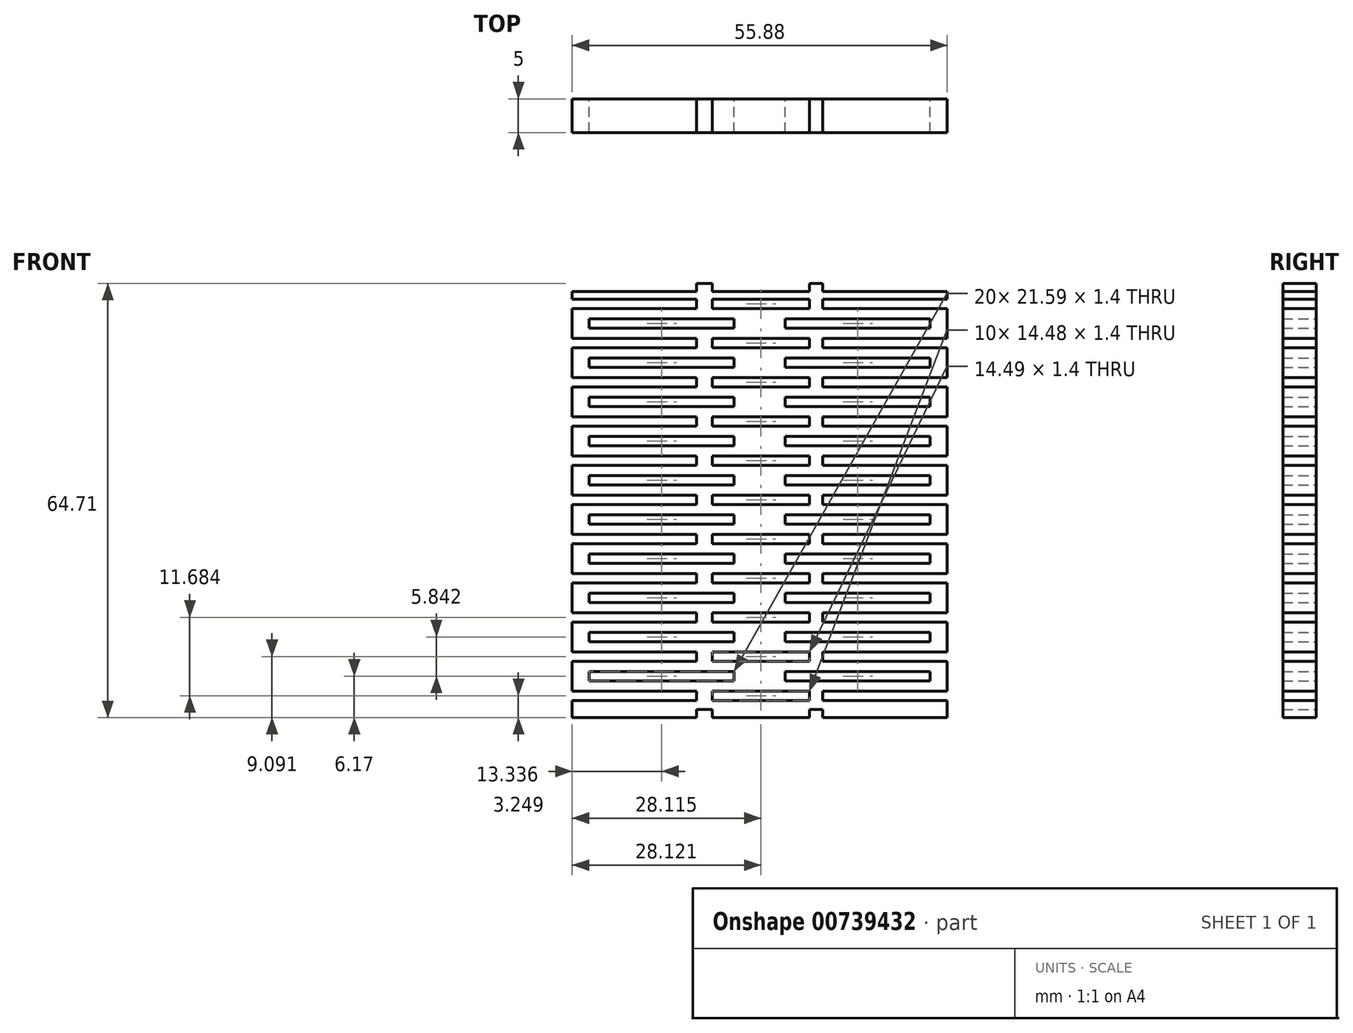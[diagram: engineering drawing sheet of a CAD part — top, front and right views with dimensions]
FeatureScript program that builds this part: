
annotation { "Feature Type Name" : "Feature", "Feature Type Description" : "" }
export const myFeature = defineFeature(function(context is Context, id is Id, definition is map)
    precondition{}
    {
        {
            var Q0;
            Q0=qCreatedBy(makeId("Front.planeOp"),FACE);
            var sketch = newSketch(context, id + "F0", { "sketchPlane" : qUnion([Q0])});
            skLineSegment(sketch, "E0", {"start": v(-42.6, 50.79) * mm, "end": v(-24.06, 50.79) * mm});
            skLineSegment(sketch, "E1", {"start": v(13.28, 50.79) * mm, "end": v(13.28, 49.63) * mm});
            skLineSegment(sketch, "E2", {"start": v(13.28, -12.71) * mm, "end": v(-5.26, -12.71) * mm});
            skLineSegment(sketch, "E3", {"start": v(-42.6, -12.71) * mm, "end": v(-42.6, -10.16) * mm});
            skPoint(sketch, "E4.start.orphan", {"position": v(-42.6, 19.04) * mm});
            skPoint(sketch, "E5.start.orphan", {"position": v(13.28, 19.04) * mm});
            skLineSegment(sketch, "E6", {"start": v(-42.6, 19.04) * mm, "end": v(-24.06, 19.04) * mm});
            skLineSegment(sketch, "E7", {"start": v(13.28, 19.04) * mm, "end": v(-5.26, 19.04) * mm});
            skLineSegment(sketch, "E8", {"start": v(-21.72, 19.04) * mm, "end": v(-7.24, 19.04) * mm});
            skLineSegment(sketch, "E9", {"start": v(-40.06, 16.13) * mm, "end": v(-18.47, 16.13) * mm});
            skLineSegment(sketch, "E10", {"start": v(10.74, 16.13) * mm, "end": v(-10.85, 16.13) * mm});
            skLineSegment(sketch, "E11", {"start": v(-24.06, 13.2) * mm, "end": v(-42.6, 13.2) * mm});
            skLineSegment(sketch, "E12", {"start": v(-21.72, 13.2) * mm, "end": v(-7.24, 13.2) * mm});
            skLineSegment(sketch, "E13", {"start": v(-5.26, 13.2) * mm, "end": v(13.28, 13.2) * mm});
            skLineSegment(sketch, "E14", {"start": v(-40.06, 10.29) * mm, "end": v(-18.47, 10.29) * mm});
            skLineSegment(sketch, "E15", {"start": v(-10.85, 10.29) * mm, "end": v(10.74, 10.29) * mm});
            skLineSegment(sketch, "E16", {"start": v(-24.06, 7.37) * mm, "end": v(-42.6, 7.37) * mm});
            skLineSegment(sketch, "E17", {"start": v(-21.72, 7.37) * mm, "end": v(-7.24, 7.37) * mm});
            skLineSegment(sketch, "E18", {"start": v(-5.26, 7.37) * mm, "end": v(13.28, 7.37) * mm});
            skLineSegment(sketch, "E19", {"start": v(-40.06, 4.45) * mm, "end": v(-18.47, 4.45) * mm});
            skLineSegment(sketch, "E20", {"start": v(-10.85, 4.45) * mm, "end": v(10.74, 4.45) * mm});
            skLineSegment(sketch, "E21", {"start": v(-24.06, 1.52) * mm, "end": v(-42.6, 1.52) * mm});
            skLineSegment(sketch, "E22", {"start": v(-21.72, 1.52) * mm, "end": v(-7.24, 1.52) * mm});
            skLineSegment(sketch, "E23", {"start": v(-5.26, 1.52) * mm, "end": v(13.28, 1.52) * mm});
            skLineSegment(sketch, "E24", {"start": v(-40.06, -1.4) * mm, "end": v(-18.47, -1.4) * mm});
            skLineSegment(sketch, "E25", {"start": v(-10.85, -1.4) * mm, "end": v(10.74, -1.4) * mm});
            skLineSegment(sketch, "E26", {"start": v(-24.06, -4.32) * mm, "end": v(-42.6, -4.32) * mm});
            skLineSegment(sketch, "E27", {"start": v(-21.72, -4.32) * mm, "end": v(-7.24, -4.32) * mm});
            skLineSegment(sketch, "E28", {"start": v(-5.26, -4.32) * mm, "end": v(13.28, -4.32) * mm});
            skLineSegment(sketch, "E29", {"start": v(-40.06, -7.24) * mm, "end": v(-18.47, -7.24) * mm});
            skLineSegment(sketch, "E30", {"start": v(-10.85, -7.24) * mm, "end": v(10.74, -7.24) * mm});
            skLineSegment(sketch, "E31", {"start": v(-24.06, -10.16) * mm, "end": v(-42.6, -10.16) * mm});
            skLineSegment(sketch, "E32", {"start": v(-21.72, -10.16) * mm, "end": v(-7.24, -10.16) * mm});
            skLineSegment(sketch, "E33", {"start": v(-5.26, -10.16) * mm, "end": v(13.28, -10.16) * mm});
            skLineSegment(sketch, "E34.MirrorCS", {"start": v(-24.06, 48.23) * mm, "end": v(-42.6, 48.23) * mm});
            skLineSegment(sketch, "E35.MirrorCS", {"start": v(-40.06, 45.31) * mm, "end": v(-18.47, 45.31) * mm});
            skLineSegment(sketch, "E36.MirrorCS", {"start": v(-24.06, 42.4) * mm, "end": v(-42.6, 42.4) * mm});
            skLineSegment(sketch, "E37.MirrorCS", {"start": v(-40.06, 39.47) * mm, "end": v(-18.47, 39.47) * mm});
            skLineSegment(sketch, "E38.MirrorCS", {"start": v(-24.06, 36.55) * mm, "end": v(-42.6, 36.55) * mm});
            skLineSegment(sketch, "E39.MirrorCS", {"start": v(-40.06, 33.63) * mm, "end": v(-18.47, 33.63) * mm});
            skLineSegment(sketch, "E40.MirrorCS", {"start": v(-24.06, 30.7) * mm, "end": v(-42.6, 30.7) * mm});
            skLineSegment(sketch, "E41.MirrorCS", {"start": v(-40.06, 27.79) * mm, "end": v(-18.47, 27.79) * mm});
            skLineSegment(sketch, "E42.MirrorCS", {"start": v(-24.06, 24.87) * mm, "end": v(-42.6, 24.87) * mm});
            skLineSegment(sketch, "E43.MirrorCS", {"start": v(-40.06, 21.95) * mm, "end": v(-18.47, 21.95) * mm});
            skLineSegment(sketch, "E44.MirrorCS", {"start": v(-21.72, 48.23) * mm, "end": v(-7.24, 48.23) * mm});
            skLineSegment(sketch, "E45.MirrorCS", {"start": v(-21.72, 42.4) * mm, "end": v(-7.24, 42.4) * mm});
            skLineSegment(sketch, "E46.MirrorCS", {"start": v(-21.72, 36.55) * mm, "end": v(-7.24, 36.55) * mm});
            skLineSegment(sketch, "E47.MirrorCS", {"start": v(-21.72, 30.7) * mm, "end": v(-7.24, 30.7) * mm});
            skLineSegment(sketch, "E48.MirrorCS", {"start": v(-21.72, 24.87) * mm, "end": v(-7.24, 24.87) * mm});
            skLineSegment(sketch, "E49.MirrorCS", {"start": v(-5.26, 48.23) * mm, "end": v(13.28, 48.23) * mm});
            skLineSegment(sketch, "E50.MirrorCS", {"start": v(-10.85, 45.31) * mm, "end": v(10.74, 45.31) * mm});
            skLineSegment(sketch, "E51.MirrorCS", {"start": v(-5.26, 42.4) * mm, "end": v(13.28, 42.4) * mm});
            skLineSegment(sketch, "E52.MirrorCS", {"start": v(-10.85, 39.47) * mm, "end": v(10.74, 39.47) * mm});
            skLineSegment(sketch, "E53.MirrorCS", {"start": v(-5.26, 36.55) * mm, "end": v(13.28, 36.55) * mm});
            skLineSegment(sketch, "E54.MirrorCS", {"start": v(-10.85, 33.63) * mm, "end": v(10.74, 33.63) * mm});
            skLineSegment(sketch, "E55.MirrorCS", {"start": v(-5.26, 30.7) * mm, "end": v(13.28, 30.7) * mm});
            skLineSegment(sketch, "E56.MirrorCS", {"start": v(-10.85, 27.79) * mm, "end": v(10.74, 27.79) * mm});
            skLineSegment(sketch, "E57.MirrorCS", {"start": v(-5.26, 24.87) * mm, "end": v(13.28, 24.87) * mm});
            skLineSegment(sketch, "E58.MirrorCS", {"start": v(10.74, 21.95) * mm, "end": v(-10.85, 21.95) * mm});
            skLineSegment(sketch, "E59", {"start": v(-24.06, 49.63) * mm, "end": v(-24.06, 48.23) * mm});
            skLineSegment(sketch, "E60", {"start": v(-24.06, 49.63) * mm, "end": v(-42.6, 49.63) * mm});
            skLineSegment(sketch, "E61", {"start": v(-18.47, 45.31) * mm, "end": v(-18.47, 46.71) * mm});
            skLineSegment(sketch, "E62", {"start": v(-18.47, 46.71) * mm, "end": v(-40.06, 46.71) * mm});
            skLineSegment(sketch, "E63", {"start": v(-40.06, 46.71) * mm, "end": v(-40.06, 45.31) * mm});
            skLineSegment(sketch, "E64", {"start": v(-24.06, 42.4) * mm, "end": v(-24.06, 43.79) * mm});
            skLineSegment(sketch, "E65", {"start": v(-24.06, 43.79) * mm, "end": v(-42.6, 43.79) * mm});
            skLineSegment(sketch, "E66", {"start": v(-18.47, 39.47) * mm, "end": v(-18.47, 40.87) * mm});
            skLineSegment(sketch, "E67", {"start": v(-18.47, 40.87) * mm, "end": v(-40.06, 40.87) * mm});
            skLineSegment(sketch, "E68", {"start": v(-40.06, 40.87) * mm, "end": v(-40.06, 39.47) * mm});
            skLineSegment(sketch, "E69", {"start": v(-24.06, 36.55) * mm, "end": v(-24.06, 37.95) * mm});
            skLineSegment(sketch, "E70", {"start": v(-24.06, 37.95) * mm, "end": v(-42.6, 37.95) * mm});
            skLineSegment(sketch, "E71", {"start": v(-18.47, 33.63) * mm, "end": v(-18.47, 35.03) * mm});
            skLineSegment(sketch, "E72", {"start": v(-18.47, 35.03) * mm, "end": v(-40.06, 35.03) * mm});
            skLineSegment(sketch, "E73", {"start": v(-40.06, 35.03) * mm, "end": v(-40.06, 33.63) * mm});
            skLineSegment(sketch, "E74", {"start": v(-24.06, 30.7) * mm, "end": v(-24.06, 32.12) * mm});
            skLineSegment(sketch, "E75", {"start": v(-24.06, 32.12) * mm, "end": v(-42.6, 32.12) * mm});
            skLineSegment(sketch, "E76", {"start": v(-18.47, 27.79) * mm, "end": v(-18.47, 29.18) * mm});
            skLineSegment(sketch, "E77", {"start": v(-18.47, 29.18) * mm, "end": v(-40.06, 29.18) * mm});
            skLineSegment(sketch, "E78", {"start": v(-40.06, 29.18) * mm, "end": v(-40.06, 27.79) * mm});
            skLineSegment(sketch, "E79", {"start": v(-24.06, 24.87) * mm, "end": v(-24.06, 26.26) * mm});
            skLineSegment(sketch, "E80", {"start": v(-24.06, 26.26) * mm, "end": v(-42.6, 26.26) * mm});
            skLineSegment(sketch, "E81", {"start": v(-18.47, 21.95) * mm, "end": v(-18.47, 23.34) * mm});
            skLineSegment(sketch, "E82", {"start": v(-18.47, 23.34) * mm, "end": v(-40.06, 23.34) * mm});
            skLineSegment(sketch, "E83", {"start": v(-40.06, 23.34) * mm, "end": v(-40.06, 21.95) * mm});
            skLineSegment(sketch, "E84", {"start": v(-24.06, 19.04) * mm, "end": v(-24.06, 20.43) * mm});
            skLineSegment(sketch, "E85", {"start": v(-24.06, 20.43) * mm, "end": v(-42.6, 20.43) * mm});
            skLineSegment(sketch, "E86", {"start": v(-18.47, 16.13) * mm, "end": v(-18.47, 17.53) * mm});
            skLineSegment(sketch, "E87", {"start": v(-18.47, 17.53) * mm, "end": v(-40.06, 17.53) * mm});
            skLineSegment(sketch, "E88", {"start": v(-40.06, 17.53) * mm, "end": v(-40.06, 16.13) * mm});
            skLineSegment(sketch, "E89", {"start": v(-24.06, 13.2) * mm, "end": v(-24.06, 14.6) * mm});
            skLineSegment(sketch, "E90", {"start": v(-24.06, 14.6) * mm, "end": v(-42.6, 14.6) * mm});
            skLineSegment(sketch, "E91", {"start": v(-18.47, 10.29) * mm, "end": v(-18.47, 11.68) * mm});
            skLineSegment(sketch, "E92", {"start": v(-18.47, 11.68) * mm, "end": v(-40.06, 11.68) * mm});
            skLineSegment(sketch, "E93", {"start": v(-40.06, 11.68) * mm, "end": v(-40.06, 10.29) * mm});
            skLineSegment(sketch, "E94", {"start": v(-24.06, 7.37) * mm, "end": v(-24.06, 8.76) * mm});
            skLineSegment(sketch, "E95", {"start": v(-24.06, 8.76) * mm, "end": v(-42.6, 8.76) * mm});
            skLineSegment(sketch, "E96", {"start": v(-18.47, 4.45) * mm, "end": v(-18.47, 5.84) * mm});
            skLineSegment(sketch, "E97", {"start": v(-18.47, 5.84) * mm, "end": v(-40.06, 5.84) * mm});
            skLineSegment(sketch, "E98", {"start": v(-40.06, 5.84) * mm, "end": v(-40.06, 4.45) * mm});
            skLineSegment(sketch, "E99", {"start": v(-24.06, 1.52) * mm, "end": v(-24.06, 2.92) * mm});
            skLineSegment(sketch, "E100", {"start": v(-24.06, 2.92) * mm, "end": v(-42.6, 2.92) * mm});
            skLineSegment(sketch, "E101", {"start": v(-18.47, -1.4) * mm, "end": v(-18.47, 0) * mm});
            skLineSegment(sketch, "E102", {"start": v(-18.47, 0) * mm, "end": v(-40.06, 0) * mm});
            skLineSegment(sketch, "E103", {"start": v(-40.06, 0) * mm, "end": v(-40.06, -1.4) * mm});
            skLineSegment(sketch, "E104", {"start": v(-24.06, -4.32) * mm, "end": v(-24.06, -2.92) * mm});
            skLineSegment(sketch, "E105", {"start": v(-24.06, -2.92) * mm, "end": v(-42.6, -2.92) * mm});
            skLineSegment(sketch, "E106", {"start": v(-18.47, -7.24) * mm, "end": v(-18.47, -5.84) * mm});
            skLineSegment(sketch, "E107", {"start": v(-18.47, -5.84) * mm, "end": v(-40.06, -5.84) * mm});
            skLineSegment(sketch, "E108", {"start": v(-40.06, -5.84) * mm, "end": v(-40.06, -7.24) * mm});
            skLineSegment(sketch, "E109", {"start": v(-24.06, -10.16) * mm, "end": v(-24.06, -8.76) * mm});
            skLineSegment(sketch, "E110", {"start": v(-24.06, -8.76) * mm, "end": v(-42.6, -8.76) * mm});
            skLineSegment(sketch, "E111", {"start": v(-7.24, 48.23) * mm, "end": v(-7.24, 49.63) * mm});
            skLineSegment(sketch, "E112", {"start": v(-7.24, 49.63) * mm, "end": v(-21.72, 49.63) * mm});
            skLineSegment(sketch, "E113", {"start": v(-21.72, 49.63) * mm, "end": v(-21.72, 48.23) * mm});
            skLineSegment(sketch, "E114", {"start": v(-7.24, 42.4) * mm, "end": v(-7.24, 43.79) * mm});
            skLineSegment(sketch, "E115", {"start": v(-7.24, 43.79) * mm, "end": v(-21.72, 43.79) * mm});
            skLineSegment(sketch, "E116", {"start": v(-21.72, 43.79) * mm, "end": v(-21.72, 42.4) * mm});
            skLineSegment(sketch, "E117", {"start": v(-7.24, 36.55) * mm, "end": v(-7.24, 37.95) * mm});
            skLineSegment(sketch, "E118", {"start": v(-7.24, 37.95) * mm, "end": v(-21.72, 37.95) * mm});
            skLineSegment(sketch, "E119", {"start": v(-21.72, 37.95) * mm, "end": v(-21.72, 36.55) * mm});
            skLineSegment(sketch, "E120", {"start": v(-7.24, 30.7) * mm, "end": v(-7.24, 32.1) * mm});
            skLineSegment(sketch, "E121", {"start": v(-7.24, 32.1) * mm, "end": v(-21.72, 32.1) * mm});
            skLineSegment(sketch, "E122", {"start": v(-21.72, 32.1) * mm, "end": v(-21.72, 30.7) * mm});
            skLineSegment(sketch, "E123", {"start": v(-7.24, 24.87) * mm, "end": v(-7.24, 26.26) * mm});
            skLineSegment(sketch, "E124", {"start": v(-7.24, 26.26) * mm, "end": v(-21.72, 26.26) * mm});
            skLineSegment(sketch, "E125", {"start": v(-21.72, 26.26) * mm, "end": v(-21.72, 24.87) * mm});
            skLineSegment(sketch, "E126", {"start": v(-7.24, 19.04) * mm, "end": v(-7.24, 20.43) * mm});
            skLineSegment(sketch, "E127", {"start": v(-7.24, 20.43) * mm, "end": v(-21.72, 20.43) * mm});
            skLineSegment(sketch, "E128", {"start": v(-21.72, 20.43) * mm, "end": v(-21.72, 19.04) * mm});
            skLineSegment(sketch, "E129", {"start": v(-7.24, 13.2) * mm, "end": v(-7.24, 14.6) * mm});
            skLineSegment(sketch, "E130", {"start": v(-7.24, 14.6) * mm, "end": v(-21.7, 14.6) * mm});
            skLineSegment(sketch, "E131", {"start": v(-21.7, 14.6) * mm, "end": v(-21.72, 13.2) * mm});
            skLineSegment(sketch, "E132", {"start": v(-7.24, 7.37) * mm, "end": v(-7.24, 8.76) * mm});
            skLineSegment(sketch, "E133", {"start": v(-7.24, 8.76) * mm, "end": v(-21.7, 8.76) * mm});
            skLineSegment(sketch, "E134", {"start": v(-21.7, 8.76) * mm, "end": v(-21.72, 7.37) * mm});
            skLineSegment(sketch, "E135", {"start": v(-7.24, 1.52) * mm, "end": v(-7.24, 2.92) * mm});
            skLineSegment(sketch, "E136", {"start": v(-7.24, 2.92) * mm, "end": v(-21.7, 2.92) * mm});
            skLineSegment(sketch, "E137", {"start": v(-21.7, 2.92) * mm, "end": v(-21.72, 1.52) * mm});
            skLineSegment(sketch, "E138", {"start": v(-7.24, -4.32) * mm, "end": v(-7.24, -2.92) * mm});
            skLineSegment(sketch, "E139", {"start": v(-7.24, -2.92) * mm, "end": v(-21.73, -2.92) * mm});
            skLineSegment(sketch, "E140", {"start": v(-21.73, -2.92) * mm, "end": v(-21.72, -4.32) * mm});
            skLineSegment(sketch, "E141", {"start": v(-7.24, -10.16) * mm, "end": v(-7.24, -8.76) * mm});
            skLineSegment(sketch, "E142", {"start": v(-7.24, -8.76) * mm, "end": v(-21.72, -8.76) * mm});
            skLineSegment(sketch, "E143", {"start": v(-21.72, -8.76) * mm, "end": v(-21.72, -10.16) * mm});
            skLineSegment(sketch, "E144", {"start": v(-5.26, 48.23) * mm, "end": v(-5.26, 49.63) * mm});
            skLineSegment(sketch, "E145", {"start": v(-5.26, 49.63) * mm, "end": v(13.28, 49.63) * mm});
            skLineSegment(sketch, "E146", {"start": v(-10.85, 45.31) * mm, "end": v(-10.85, 46.71) * mm});
            skLineSegment(sketch, "E147", {"start": v(-10.85, 46.71) * mm, "end": v(10.74, 46.71) * mm});
            skLineSegment(sketch, "E148", {"start": v(10.74, 46.71) * mm, "end": v(10.74, 45.31) * mm});
            skLineSegment(sketch, "E149", {"start": v(-5.26, 42.4) * mm, "end": v(-5.26, 43.79) * mm});
            skLineSegment(sketch, "E150", {"start": v(-5.26, 43.79) * mm, "end": v(13.28, 43.79) * mm});
            skLineSegment(sketch, "E151", {"start": v(-10.85, 39.47) * mm, "end": v(-10.85, 40.87) * mm});
            skLineSegment(sketch, "E152", {"start": v(-10.85, 40.87) * mm, "end": v(10.74, 40.87) * mm});
            skLineSegment(sketch, "E153", {"start": v(10.74, 40.87) * mm, "end": v(10.74, 39.47) * mm});
            skLineSegment(sketch, "E154", {"start": v(-5.26, 36.55) * mm, "end": v(-5.26, 37.95) * mm});
            skLineSegment(sketch, "E155", {"start": v(-5.26, 37.95) * mm, "end": v(13.28, 37.95) * mm});
            skLineSegment(sketch, "E156", {"start": v(-10.85, 33.63) * mm, "end": v(-10.85, 35.03) * mm});
            skLineSegment(sketch, "E157", {"start": v(-10.85, 35.03) * mm, "end": v(10.74, 35.03) * mm});
            skLineSegment(sketch, "E158", {"start": v(10.74, 35.03) * mm, "end": v(10.74, 33.63) * mm});
            skLineSegment(sketch, "E159", {"start": v(-5.26, 30.7) * mm, "end": v(-5.26, 32.11) * mm});
            skLineSegment(sketch, "E160", {"start": v(-5.26, 32.11) * mm, "end": v(13.28, 32.11) * mm});
            skLineSegment(sketch, "E161", {"start": v(-10.85, 27.79) * mm, "end": v(-10.85, 29.18) * mm});
            skLineSegment(sketch, "E162", {"start": v(-10.85, 29.18) * mm, "end": v(10.74, 29.18) * mm});
            skLineSegment(sketch, "E163", {"start": v(10.74, 29.18) * mm, "end": v(10.74, 27.79) * mm});
            skLineSegment(sketch, "E164", {"start": v(-5.26, 24.87) * mm, "end": v(-5.26, 26.26) * mm});
            skLineSegment(sketch, "E165", {"start": v(-5.26, 26.26) * mm, "end": v(13.28, 26.26) * mm});
            skLineSegment(sketch, "E166", {"start": v(-10.85, 21.95) * mm, "end": v(-10.85, 23.34) * mm});
            skLineSegment(sketch, "E167", {"start": v(-10.85, 23.34) * mm, "end": v(10.74, 23.34) * mm});
            skLineSegment(sketch, "E168", {"start": v(10.74, 23.34) * mm, "end": v(10.74, 21.95) * mm});
            skLineSegment(sketch, "E169", {"start": v(-5.26, 19.04) * mm, "end": v(-5.26, 20.43) * mm});
            skLineSegment(sketch, "E170", {"start": v(-5.26, 20.43) * mm, "end": v(13.28, 20.43) * mm});
            skLineSegment(sketch, "E171", {"start": v(-10.85, 16.13) * mm, "end": v(-10.85, 17.53) * mm});
            skLineSegment(sketch, "E172", {"start": v(-10.85, 17.53) * mm, "end": v(10.74, 17.53) * mm});
            skLineSegment(sketch, "E173", {"start": v(10.74, 17.53) * mm, "end": v(10.74, 16.13) * mm});
            skLineSegment(sketch, "E174", {"start": v(-5.26, 13.2) * mm, "end": v(-5.26, 14.6) * mm});
            skLineSegment(sketch, "E175", {"start": v(-5.26, 14.6) * mm, "end": v(13.28, 14.6) * mm});
            skLineSegment(sketch, "E176", {"start": v(-10.85, 10.29) * mm, "end": v(-10.85, 11.68) * mm});
            skLineSegment(sketch, "E177", {"start": v(-10.85, 11.68) * mm, "end": v(10.74, 11.68) * mm});
            skLineSegment(sketch, "E178", {"start": v(10.74, 11.68) * mm, "end": v(10.74, 10.29) * mm});
            skLineSegment(sketch, "E179", {"start": v(-5.26, 7.37) * mm, "end": v(-5.26, 8.76) * mm});
            skLineSegment(sketch, "E180", {"start": v(-5.26, 8.76) * mm, "end": v(13.28, 8.76) * mm});
            skLineSegment(sketch, "E181", {"start": v(-10.85, 4.45) * mm, "end": v(-10.85, 5.84) * mm});
            skLineSegment(sketch, "E182", {"start": v(-10.85, 5.84) * mm, "end": v(10.74, 5.84) * mm});
            skLineSegment(sketch, "E183", {"start": v(10.74, 5.84) * mm, "end": v(10.74, 4.45) * mm});
            skLineSegment(sketch, "E184", {"start": v(-5.26, 1.52) * mm, "end": v(-5.26, 2.92) * mm});
            skLineSegment(sketch, "E185", {"start": v(-5.26, 2.92) * mm, "end": v(13.28, 2.92) * mm});
            skLineSegment(sketch, "E186", {"start": v(-10.85, -1.4) * mm, "end": v(-10.85, 0) * mm});
            skLineSegment(sketch, "E187", {"start": v(-10.85, 0) * mm, "end": v(10.74, 0) * mm});
            skLineSegment(sketch, "E188", {"start": v(10.74, 0) * mm, "end": v(10.74, -1.4) * mm});
            skLineSegment(sketch, "E189", {"start": v(-5.26, -4.32) * mm, "end": v(-5.26, -2.92) * mm});
            skLineSegment(sketch, "E190", {"start": v(-5.26, -2.92) * mm, "end": v(13.28, -2.92) * mm});
            skLineSegment(sketch, "E191", {"start": v(-10.85, -7.24) * mm, "end": v(-10.85, -5.84) * mm});
            skLineSegment(sketch, "E192", {"start": v(-10.85, -5.84) * mm, "end": v(10.74, -5.84) * mm});
            skLineSegment(sketch, "E193", {"start": v(10.74, -5.84) * mm, "end": v(10.74, -7.24) * mm});
            skLineSegment(sketch, "E194", {"start": v(-5.26, -10.16) * mm, "end": v(-5.26, -8.76) * mm});
            skLineSegment(sketch, "E195", {"start": v(-5.26, -8.76) * mm, "end": v(13.28, -8.76) * mm});
            skLineSegment(sketch, "E196.trimOffspring", {"start": v(-42.6, 49.63) * mm, "end": v(-42.6, 50.79) * mm});
            skLineSegment(sketch, "E197.trimOffspring", {"start": v(-42.6, 43.79) * mm, "end": v(-42.6, 48.23) * mm});
            skLineSegment(sketch, "E198.trimOffspring", {"start": v(-42.6, 37.95) * mm, "end": v(-42.6, 42.4) * mm});
            skLineSegment(sketch, "E199.trimOffspring", {"start": v(-42.6, 32.12) * mm, "end": v(-42.6, 36.55) * mm});
            skLineSegment(sketch, "E200.trimOffspring", {"start": v(-42.6, 26.26) * mm, "end": v(-42.6, 30.7) * mm});
            skLineSegment(sketch, "E201.trimOffspring", {"start": v(-42.6, 20.43) * mm, "end": v(-42.6, 24.87) * mm});
            skLineSegment(sketch, "E202.trimOffspring", {"start": v(-42.6, 14.6) * mm, "end": v(-42.6, 19.04) * mm});
            skLineSegment(sketch, "E203.trimOffspring", {"start": v(-42.6, 8.76) * mm, "end": v(-42.6, 13.2) * mm});
            skLineSegment(sketch, "E204.trimOffspring", {"start": v(-42.6, 2.92) * mm, "end": v(-42.6, 7.37) * mm});
            skLineSegment(sketch, "E205.trimOffspring", {"start": v(-42.6, -2.92) * mm, "end": v(-42.6, 1.52) * mm});
            skLineSegment(sketch, "E206.trimOffspring", {"start": v(-42.6, -8.76) * mm, "end": v(-42.6, -4.32) * mm});
            skLineSegment(sketch, "E207.trimOffspring", {"start": v(13.28, 48.23) * mm, "end": v(13.28, 43.79) * mm});
            skLineSegment(sketch, "E208.trimOffspring", {"start": v(13.28, 42.4) * mm, "end": v(13.28, 37.95) * mm});
            skLineSegment(sketch, "E209.trimOffspring", {"start": v(13.28, 36.55) * mm, "end": v(13.28, 32.11) * mm});
            skLineSegment(sketch, "E210.trimOffspring", {"start": v(13.28, 30.7) * mm, "end": v(13.28, 26.26) * mm});
            skLineSegment(sketch, "E211.trimOffspring", {"start": v(13.28, 24.87) * mm, "end": v(13.28, 20.43) * mm});
            skLineSegment(sketch, "E212.trimOffspring", {"start": v(13.28, 19.04) * mm, "end": v(13.28, 14.6) * mm});
            skLineSegment(sketch, "E213.trimOffspring", {"start": v(13.28, 13.2) * mm, "end": v(13.28, 8.76) * mm});
            skLineSegment(sketch, "E214.trimOffspring", {"start": v(13.28, 7.37) * mm, "end": v(13.28, 2.92) * mm});
            skLineSegment(sketch, "E215.trimOffspring", {"start": v(13.28, 1.52) * mm, "end": v(13.28, -2.92) * mm});
            skLineSegment(sketch, "E216.trimOffspring", {"start": v(13.28, -4.32) * mm, "end": v(13.28, -8.76) * mm});
            skLineSegment(sketch, "E217.trimOffspring", {"start": v(13.28, -10.16) * mm, "end": v(13.28, -12.71) * mm});
            skLineSegment(sketch, "E218", {"start": v(-24.06, 50.79) * mm, "end": v(-24.06, 52) * mm});
            skLineSegment(sketch, "E219", {"start": v(-24.06, 52) * mm, "end": v(-21.72, 52) * mm});
            skLineSegment(sketch, "E220", {"start": v(-21.72, 52) * mm, "end": v(-21.72, 50.79) * mm});
            skLineSegment(sketch, "E221", {"start": v(-7.24, 50.79) * mm, "end": v(-7.24, 52) * mm});
            skLineSegment(sketch, "E222", {"start": v(-7.24, 52) * mm, "end": v(-5.26, 52) * mm});
            skLineSegment(sketch, "E223", {"start": v(-5.26, 52) * mm, "end": v(-5.26, 50.79) * mm});
            skLineSegment(sketch, "E224", {"start": v(-24.06, -12.71) * mm, "end": v(-24.06, -11.5) * mm});
            skLineSegment(sketch, "E225", {"start": v(-24.06, -11.5) * mm, "end": v(-21.72, -11.5) * mm});
            skLineSegment(sketch, "E226", {"start": v(-21.72, -11.5) * mm, "end": v(-21.72, -12.71) * mm});
            skLineSegment(sketch, "E227", {"start": v(-7.24, -12.71) * mm, "end": v(-7.24, -11.5) * mm});
            skLineSegment(sketch, "E228", {"start": v(-7.24, -11.5) * mm, "end": v(-5.26, -11.5) * mm});
            skLineSegment(sketch, "E229", {"start": v(-5.26, -11.5) * mm, "end": v(-5.26, -12.71) * mm});
            skLineSegment(sketch, "E230.trimOffspring", {"start": v(-24.06, -12.71) * mm, "end": v(-42.6, -12.71) * mm});
            skLineSegment(sketch, "E231.trimOffspring", {"start": v(-7.24, -12.71) * mm, "end": v(-21.72, -12.71) * mm});
            skLineSegment(sketch, "E232.trimOffspring", {"start": v(-21.72, 50.79) * mm, "end": v(-7.24, 50.79) * mm});
            skLineSegment(sketch, "E233.trimOffspring", {"start": v(-5.26, 50.79) * mm, "end": v(13.28, 50.79) * mm});
            skSolve(sketch);
        }
        {
            var Q0;
            Q0=makeQuery(id+"F0.imprint","IMPRINT",FACE,{"disambiguationData":[TD([[makeQuery(id+"F0.imprint","IMPRINT",EDGE,{"derivedFrom":sQuery(id+"F0.wireOp",EDGE,"E0")}),-1.0]])]});
            extrude(context, id + "F1", {"entities" : qUnion([Q0]), "depth" : 5 * mm, "offsetDistance" : 25 * mm});
        }
    });
